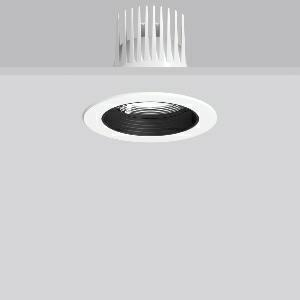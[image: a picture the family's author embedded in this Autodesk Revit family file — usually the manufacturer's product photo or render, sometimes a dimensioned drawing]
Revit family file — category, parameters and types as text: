
# Revit family: heledon_maxi_e_901768_002_1_76_7f23
name_source: partatom
category: Lighting Fixtures
units: mm (PartAtom-declared; Revit-internal decimal feet)

## family parameters
Cut with Voids When Loaded = No
Host = Face
Light Source = No
Part Type = Normal
Room Calculation Point = No
Round Connector Dimension = Use Diameter
Shared = No

## types (1)
- HELEDON maxi E (1 x LED Modul 940, 3750 lm, 4000)
    Apparent Load = 35 VA
    Approval mark = CE
    CIE Flux Codes = 96 100 100 100 100
    Color Rendering = 92
    Color Temperature = 4000
    Default Elevation = 1800 mm
    Description = Series: HELEDON maxi
Round recessed downlight. Housing: die-cast aluminium, powder-coated. Black plastic ring and recessed LED to prevent glare from the side. Optical assembly with lens made of plastic (polycarbonate) for the best homogeneous light distribution - can be changed without tools. Best colour rendering index Ra>90. Suitable for Recessed ceiling mounting. Installation without tools thanks to spring fastening system. Including separate LED converter with connecting cable 600 mm.High quality converter without flickering and stroboscopic effect. Through-wiring box (5 pole) available as accessory. The following accessories can be mounted without use of tools: interchangeable lenses, decorative glasses, honeycomb louvre, clear and frosted diffusers, white interchangeable plastic ring. 
Colour: traffic white, matt (RAL 9016)
Diameter: 162 mm
Height: 3 mm
Cut-out diameter: 152 mm
Recess height: 200 mm
Luminaire: recess height: 135 mm
Lamp: LED
Socket: without socket
Colour temperature: 4000K
Colour rendering index (CRI): 92
System power: 35 W
Rated luminous flux: 3750 lm
Luminous efficiency: 107 lm/W
Control gear: Converter, dimmable, DALI
Protection class: II
Type of protection: IP 20
    Height = 0 mm  [stored 0 ft]
    Lamp = 1 x LED Modul 940
    Lamp Light Flux = 3750 lm
    Lamp count = 1
    Length = 162 mm
    Lifetime = 50000 h
    Luminous efficacy = 107 lm/W
    Manufacturer = RZB
    ModVariant = No
    Model = 901768.002.1.76
    Mounting Place = Ceiling
    Mounting Type = Recessed
    Number of Poles = 1
    OnlyDefault = Yes
    Power Factor = 1
    Product Name = HELEDON maxi E
    Product group = Recessed downlights
    ProductGroupID = 402
    Protection Class = Protection class II
    Protection Degree = IP 20
    RLX_Detail_Level = 1
    RLX_Emergency_Light_Flux = 0 lm
    RLX_Emergency_Type = 0
    RLX_Emergency_Type_DB = No
    RlxData = <blob elided: 120105 chars, md5=cd9204f8>
    Socket = socket
    Standby Power = 0 W
    System Light Flux = 3750 lm
    System Power = 35 W
    Type Comments = Product without accessories
    Type Image = 901663.002.jpg
    URL = http://relux.com
    VarID = ---
    Voltage = 230 V
    Voltage Range = 220-240 V
    Weight = 0.00 kg
    Width = 0 mm  [stored 0 ft]

note: [stored X ft] marks values corroborated as IEEE doubles in the binary element streams (Revit-internal decimal feet)

## geometry (parser evidence)
native form markers: Blend x4, Sweep x11
no freeform markers — native parametric forms only
